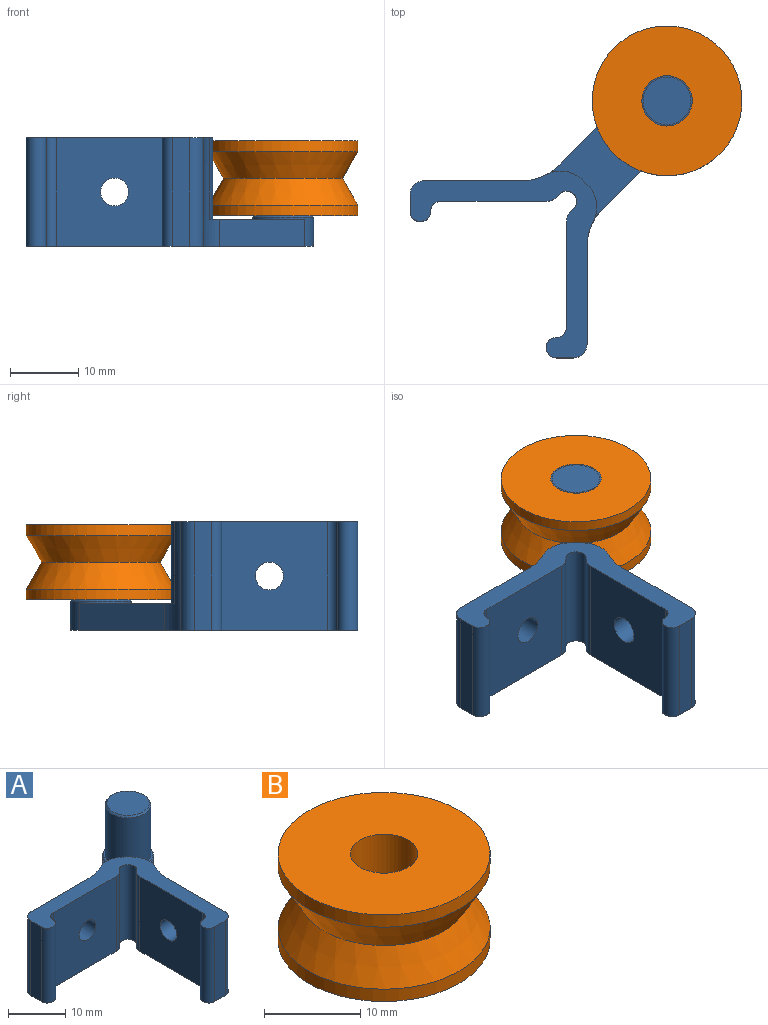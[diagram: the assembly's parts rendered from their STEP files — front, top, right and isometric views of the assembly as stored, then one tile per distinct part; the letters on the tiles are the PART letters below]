
ASSEMBLY  parts=2 mates=1
PART A: 35 faces, bbox 42.2x42.2x16 mm
  f0: cylinder r=1.5mm len=16mm, axis (0,0,-1), area 37.7mm2, adj f1,f21,f23,f32
  f1: plane 16x15.55mm, normal (0,-1,0), area 235.6mm2, adj f0,f2,f23,f32,f33
  f2: cylinder r=2mm len=16mm, axis (0,0,-1), area 25.1mm2, adj f1,f3,f23,f32
  f3: plane 16x0.48mm, normal (0.71,-0.71,0), area 10.7mm2, adj f2,f4,f23,f32
  f4: cylinder r=1.5mm len=16mm, axis (0,0,-1), area 75.4mm2, adj f3,f5,f23,f32
  f5: plane 16x0.48mm, normal (-0.71,0.71,0), area 10.7mm2, adj f4,f6,f23,f32
  f6: cylinder r=2mm len=16mm, axis (0,0,-1), area 25.1mm2, adj f5,f7,f23,f32
  f7: plane 16x15.55mm, normal (-1,0,0), area 235.6mm2, adj f6,f8,f23,f32,f34
  f8: cylinder r=1.5mm len=16mm, axis (0,0,-1), area 37.7mm2, adj f7,f9,f23,f32
  f9: cylinder r=1.5mm len=16mm, axis (0,0,-1), area 75.4mm2, adj f8,f10,f23,f32
  f10: plane 16x2.5mm, normal (0,-1,0), area 40mm2, adj f9,f11,f23,f32
  f11: cylinder r=2mm len=16mm, axis (0,0,-1), area 50.3mm2, adj f10,f12,f23,f32
  f12: plane 16x14.32mm, normal (1,0,0), area 216mm2, adj f11,f13,f23,f32,f34
  f13: cylinder r=8mm len=16mm, axis (0,0,-1), area 71.7mm2, adj f12,f14,f22,f23,f29,f32
  f14: plane 12.59x12.59mm, normal (0.71,-0.71,0), area 71.2mm2, adj f13,f15,f22,f23
  f15: cylinder r=4.5mm len=9mm, axis (0,0,-1), area 65mm2, adj f14,f16,f22,f23,f25
  f16: plane 12.59x12.59mm, normal (-0.71,0.71,0), area 71.2mm2, adj f15,f17,f22,f23
  f17: cylinder r=8mm len=16mm, axis (0,0,-1), area 71.7mm2, adj f16,f18,f22,f23,f31,f32
  f18: plane 16x14.32mm, normal (0,1,0), area 216mm2, adj f17,f19,f23,f32,f33
  f19: cylinder r=2mm len=16mm, axis (0,0,-1), area 50.3mm2, adj f18,f20,f23,f32
  f20: plane 16x2.5mm, normal (-1,0,0), area 40mm2, adj f19,f21,f23,f32
  f21: cylinder r=1.5mm len=16mm, axis (0,0,-1), area 75.4mm2, adj f0,f20,f23,f32
  f22: plane 20.88x20.88mm, normal (0,0,1), area 126.7mm2, adj f13,f14,f15,f16,f17,f29,f30,f31
  f23: plane 42.25x42.25mm, normal (0,0,-1), area 360.7mm2, adj f0,f1,f2,f3,f4,f5,f6,f7
  f24: plane 8.6x8.6mm, normal (0,0,1), area 7.8mm2, adj f25,f26
  f25: cone r=4.3mm half-angle=45deg, axis (0,0,-1), area 7.8mm2, adj f15,f24
  f26: cylinder r=4mm len=10.7mm, axis (0,0,-1), area 268.9mm2, adj f24,f28
  f27: plane 7.4x7.4mm, normal (0,0,1), area 43mm2, adj f28
  f28: cone r=3.7mm half-angle=45deg, axis (0,0,-1), area 10.3mm2, adj f26,f27
  f29: cylinder r=4.5mm len=12mm, axis (0,0,-1), area 68.7mm2, adj f13,f22,f30,f32
  f30: plane 12x0.79mm, normal (0.71,0.71,0), area 13.4mm2, adj f22,f29,f31,f32
  f31: cylinder r=4.5mm len=12mm, axis (0,0,-1), area 68.7mm2, adj f17,f22,f30,f32
  f32: plane 27.44x27.44mm, normal (0,0,1), area 170.4mm2, adj f0,f1,f2,f3,f4,f5,f6,f7
  f33: cylinder r=2.05mm len=4.1mm, axis (0,1,0), area 38.6mm2, adj f1,f18
  f34: cylinder r=2.05mm len=4.1mm, axis (1,0,0), area 38.6mm2, adj f7,f12
PART B: 7 faces, bbox 22x22x11 mm
  f0: cylinder r=11mm len=22mm, axis (0,0,1), area 108mm2, adj f1,f6
  f1: plane 22x22mm, normal (0,0,-1), area 341.6mm2, adj f0,f2
  f2: cylinder r=3.5mm len=11mm, axis (0,0,1), area 241.9mm2, adj f1,f3
  f3: plane 22x22mm, normal (0,0,1), area 341.6mm2, adj f2,f4
  f4: cylinder r=11mm len=22mm, axis (0,0,1), area 108mm2, adj f3,f5
  f5: cone r=11mm half-angle=30deg, axis (0,0,1), area 281.8mm2, adj f4,f6
  f6: cone r=8.73mm half-angle=30deg, axis (0,0,-1), area 281.8mm2, adj f0,f5
PLACE A t=(-21.08,14.63,4.88)mm
PLACE B t=(3.67,39.38,14.88)mm
MATE revolute A.f15 <-> B.f0  axis (0,0,1) through (3.67,39.38,9.38)mm
